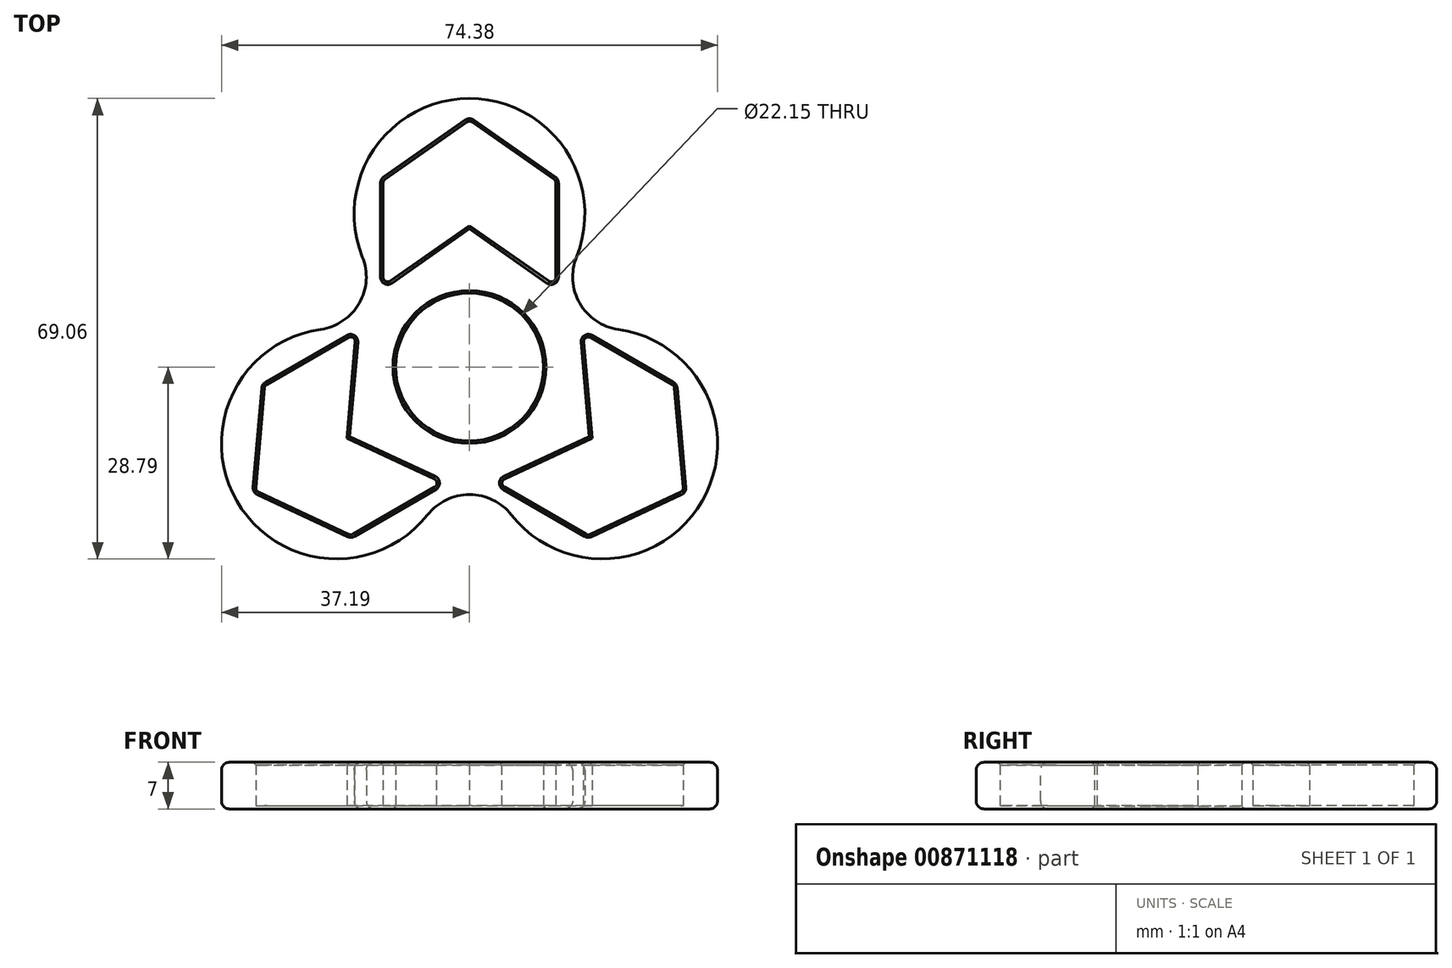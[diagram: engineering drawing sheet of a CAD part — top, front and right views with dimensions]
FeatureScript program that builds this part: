
annotation { "Feature Type Name" : "Feature", "Feature Type Description" : "" }
export const myFeature = defineFeature(function(context is Context, id is Id, definition is map)
    precondition{}
    {
        {
            var Q0;
            Q0=qCreatedBy(makeId("Top.planeOp"),FACE);
            var sketch = newSketch(context, id + "F0", { "sketchPlane" : qUnion([Q0])});
            skCircle(sketch, "E0", {"center": v(0, 0) * mm, "radius": 11.07 * mm});
            skCircle(sketch, "E1", {"center": v(0, 0) * mm, "radius": 26.5 * mm, "construction": true});
            skArc(sketch, "E2", {"start": v(-13.1, 23.03) * mm, "mid": v(-13.03, 22.75) * mm, "end": v(-12.95, 22.47) * mm, "construction": true});
            skLineSegment(sketch, "E3", {"start": v(0, 43.45) * mm, "end": v(0, 0) * mm});
            skLineSegment(sketch, "E4", {"start": v(0, 37) * mm, "end": v(12.95, 27.94) * mm});
            skLineSegment(sketch, "E5", {"start": v(12.95, 27.94) * mm, "end": v(12.95, 12.13) * mm});
            skLineSegment(sketch, "E6", {"start": v(12.95, 12.13) * mm, "end": v(0, 21.2) * mm});
            skLineSegment(sketch, "E7.MirrorCS", {"start": v(0, 37) * mm, "end": v(-12.95, 27.94) * mm});
            skLineSegment(sketch, "E8.MirrorCS", {"start": v(-12.95, 27.94) * mm, "end": v(-12.95, 12.13) * mm});
            skLineSegment(sketch, "E9.MirrorCS", {"start": v(-12.95, 12.13) * mm, "end": v(0, 21.2) * mm});
            skLineSegment(sketch, "E10.1.0", {"start": v(-32.1, -18.57) * mm, "end": v(-17.76, -25.25) * mm});
            skLineSegment(sketch, "E10.1.1", {"start": v(-17.76, -25.25) * mm, "end": v(-4.07, -17.35) * mm});
            skLineSegment(sketch, "E10.1.2", {"start": v(-4.07, -17.35) * mm, "end": v(-18.4, -10.67) * mm});
            skLineSegment(sketch, "E10.1.3", {"start": v(-17.02, 5.08) * mm, "end": v(-18.4, -10.67) * mm});
            skLineSegment(sketch, "E10.1.4", {"start": v(-30.71, -2.82) * mm, "end": v(-17.02, 5.08) * mm});
            skLineSegment(sketch, "E10.1.5", {"start": v(-32.1, -18.57) * mm, "end": v(-30.71, -2.82) * mm});
            skLineSegment(sketch, "E10.2.0", {"start": v(32.1, -18.57) * mm, "end": v(30.71, -2.82) * mm});
            skLineSegment(sketch, "E10.2.1", {"start": v(30.71, -2.82) * mm, "end": v(17.02, 5.08) * mm});
            skLineSegment(sketch, "E10.2.2", {"start": v(17.02, 5.08) * mm, "end": v(18.4, -10.67) * mm});
            skLineSegment(sketch, "E10.2.3", {"start": v(4.07, -17.35) * mm, "end": v(18.4, -10.67) * mm});
            skLineSegment(sketch, "E10.2.4", {"start": v(17.76, -25.25) * mm, "end": v(4.07, -17.35) * mm});
            skLineSegment(sketch, "E10.2.5", {"start": v(32.1, -18.57) * mm, "end": v(17.76, -25.25) * mm});
            skPoint(sketch, "E10.center", {"position": v(0, -0.05) * mm});
            skArc(sketch, "E11.trimOffspring", {"start": v(12.95, 22.47) * mm, "mid": v(13, 22.77) * mm, "end": v(13.05, 23.06) * mm, "construction": true});
            skCircle(sketch, "E12", {"center": v(0, 22.97) * mm, "radius": 17.3 * mm});
            skCircle(sketch, "E13.1.0", {"center": v(-19.9, -11.48) * mm, "radius": 17.3 * mm});
            skCircle(sketch, "E13.2.0", {"center": v(19.9, -11.48) * mm, "radius": 17.3 * mm});
            skLineSegment(sketch, "E14", {"start": v(-17.02, 5.08) * mm, "end": v(-12.95, 12.13) * mm});
            skLineSegment(sketch, "E15", {"start": v(12.95, 12.13) * mm, "end": v(17.02, 5.08) * mm});
            skLineSegment(sketch, "E16", {"start": v(4.07, -17.35) * mm, "end": v(-4.07, -17.35) * mm});
            skLineSegment(sketch, "E17", {"start": v(-7.18, -19.14) * mm, "end": v(7.18, -19.14) * mm});
            skLineSegment(sketch, "E18.1.0", {"start": v(20.13, 3.3) * mm, "end": v(12.96, 15.73) * mm});
            skLineSegment(sketch, "E18.2.0", {"start": v(-12.96, 15.73) * mm, "end": v(-20.13, 3.3) * mm});
            skPoint(sketch, "E18.center", {"position": v(0, -0.03) * mm});
            skSolve(sketch);
        }
        {
            var Q0;
            {var subQ1=sQuery(id+"F0.wireOp",EDGE,"E7.MirrorCS");Q0=makeQuery(id+"F0.imprint","IMPRINT",FACE,{"disambiguationData":[TD([[makeQuery(id+"F0.imprint","IMPRINT",EDGE,{"derivedFrom":subQ1}),-1.0]])]});}
            var Q1;
            {var subQ0=sQuery(id+"F0.wireOp",EDGE,"E4");Q1=makeQuery(id+"F0.imprint","IMPRINT",FACE,{"disambiguationData":[TD([[makeQuery(id+"F0.imprint","IMPRINT",EDGE,{"derivedFrom":subQ0}),1.0]])]});}
            var Q2;
            {var subQ5=sQuery(id+"F0.wireOp",EDGE,"E6");Q2=makeQuery(id+"F0.imprint","IMPRINT",FACE,{"disambiguationData":[TD([[makeQuery(id+"F0.imprint","IMPRINT",EDGE,{"derivedFrom":subQ5}),1.0]])]});}
            var Q3;
            {var subQ0=sQuery(id+"F0.wireOp",EDGE,"E9.MirrorCS");Q3=makeQuery(id+"F0.imprint","IMPRINT",FACE,{"disambiguationData":[TD([[makeQuery(id+"F0.imprint","IMPRINT",EDGE,{"derivedFrom":subQ0}),-1.0]])]});}
            var Q4;
            {var subQ0=sQuery(id+"F0.wireOp",EDGE,"E12");var subQ1=sQuery(id+"F0.wireOp",EDGE,"E0");var subQ2=makeQuery(id+"F0.imprint","INTERSECT",VERTEX,{"disambiguationData":[OD(1.0)],"derivedFrom":[subQ1,subQ0]});Q4=makeQuery(id+"F0.imprint","IMPRINT",FACE,{"disambiguationData":[TD([[makeQuery(id+"F0.imprint","IMPRINT",EDGE,{"disambiguationData":[TD([[subQ2,-1.0]])],"derivedFrom":subQ1}),-1.0]])]});}
            var Q5;
            {var subQ1=sQuery(id+"F0.wireOp",EDGE,"E10.1.2");Q5=makeQuery(id+"F0.imprint","IMPRINT",FACE,{"disambiguationData":[TD([[makeQuery(id+"F0.imprint","IMPRINT",EDGE,{"derivedFrom":subQ1}),-1.0]])]});}
            var Q6;
            {var subQ0=sQuery(id+"F0.wireOp",EDGE,"E13.1.0");var subQ1=sQuery(id+"F0.wireOp",EDGE,"E0");var subQ2=makeQuery(id+"F0.imprint","INTERSECT",VERTEX,{"disambiguationData":[OD(1.0)],"derivedFrom":[subQ1,subQ0]});Q6=makeQuery(id+"F0.imprint","IMPRINT",FACE,{"disambiguationData":[TD([[makeQuery(id+"F0.imprint","IMPRINT",EDGE,{"disambiguationData":[TD([[subQ2,-1.0]])],"derivedFrom":subQ1}),-1.0]])]});}
            var Q7;
            {var subQ9=sQuery(id+"F0.wireOp",EDGE,"E10.2.2");Q7=makeQuery(id+"F0.imprint","IMPRINT",FACE,{"disambiguationData":[TD([[makeQuery(id+"F0.imprint","IMPRINT",EDGE,{"derivedFrom":subQ9}),-1.0]])]});}
            var Q8;
            {var subQ0=sQuery(id+"F0.wireOp",EDGE,"E12");var subQ1=sQuery(id+"F0.wireOp",EDGE,"E0");var subQ2=makeQuery(id+"F0.imprint","INTERSECT",VERTEX,{"disambiguationData":[OD(0.0)],"derivedFrom":[subQ1,subQ0]});Q8=makeQuery(id+"F0.imprint","IMPRINT",FACE,{"disambiguationData":[TD([[makeQuery(id+"F0.imprint","IMPRINT",EDGE,{"disambiguationData":[TD([[subQ2,1.0]])],"derivedFrom":subQ1}),-1.0]])]});}
            var Q9;
            {var subQ6=sQuery(id+"F0.wireOp",EDGE,"E10.2.0");Q9=makeQuery(id+"F0.imprint","IMPRINT",FACE,{"disambiguationData":[TD([[makeQuery(id+"F0.imprint","IMPRINT",EDGE,{"derivedFrom":subQ6}),-1.0]])]});}
            var Q10;
            {var subQ7=sQuery(id+"F0.wireOp",EDGE,"E10.1.0");Q10=makeQuery(id+"F0.imprint","IMPRINT",FACE,{"disambiguationData":[TD([[makeQuery(id+"F0.imprint","IMPRINT",EDGE,{"derivedFrom":subQ7}),-1.0]])]});}
            var Q11;
            {var subQ0=sQuery(id+"F0.wireOp",EDGE,"E18.2.0");var subQ1=sQuery(id+"F0.wireOp",EDGE,"E12");var subQ2=makeQuery(id+"F0.imprint","INTERSECT",VERTEX,{"derivedFrom":[subQ1,subQ0]});Q11=makeQuery(id+"F0.imprint","IMPRINT",FACE,{"disambiguationData":[TD([[makeQuery(id+"F0.imprint","IMPRINT",EDGE,{"disambiguationData":[TD([[subQ2,-1.0]])],"derivedFrom":subQ1}),-1.0]])]});}
            var Q12;
            {var subQ0=sQuery(id+"F0.wireOp",EDGE,"E17");var subQ1=sQuery(id+"F0.wireOp",EDGE,"E13.1.0");var subQ2=makeQuery(id+"F0.imprint","INTERSECT",VERTEX,{"derivedFrom":[subQ1,subQ0]});Q12=makeQuery(id+"F0.imprint","IMPRINT",FACE,{"disambiguationData":[TD([[makeQuery(id+"F0.imprint","IMPRINT",EDGE,{"disambiguationData":[TD([[subQ2,-1.0]])],"derivedFrom":subQ1}),-1.0]])]});}
            var Q13;
            {var subQ3=sQuery(id+"F0.wireOp",EDGE,"E18.2.0");var subQ5=sQuery(id+"F0.wireOp",EDGE,"E12");var subQ7=makeQuery(id+"F0.imprint","INTERSECT",VERTEX,{"derivedFrom":[subQ5,subQ3]});Q13=makeQuery(id+"F0.imprint","IMPRINT",FACE,{"disambiguationData":[TD([[makeQuery(id+"F0.imprint","IMPRINT",EDGE,{"disambiguationData":[TD([[subQ7,-1.0]])],"derivedFrom":subQ5}),1.0]])]});}
            var Q14;
            {var subQ3=sQuery(id+"F0.wireOp",EDGE,"E18.2.0");var subQ5=sQuery(id+"F0.wireOp",EDGE,"E13.1.0");var subQ7=makeQuery(id+"F0.imprint","INTERSECT",VERTEX,{"derivedFrom":[subQ5,subQ3]});Q14=makeQuery(id+"F0.imprint","IMPRINT",FACE,{"disambiguationData":[TD([[makeQuery(id+"F0.imprint","IMPRINT",EDGE,{"disambiguationData":[TD([[subQ7,1.0]])],"derivedFrom":subQ5}),1.0]])]});}
            var Q15;
            {var subQ3=sQuery(id+"F0.wireOp",EDGE,"E17");var subQ5=sQuery(id+"F0.wireOp",EDGE,"E13.1.0");var subQ6=makeQuery(id+"F0.imprint","INTERSECT",VERTEX,{"derivedFrom":[subQ5,subQ3]});Q15=makeQuery(id+"F0.imprint","IMPRINT",FACE,{"disambiguationData":[TD([[makeQuery(id+"F0.imprint","IMPRINT",EDGE,{"disambiguationData":[TD([[subQ6,-1.0]])],"derivedFrom":subQ5}),1.0]])]});}
            var Q16;
            {var subQ3=sQuery(id+"F0.wireOp",EDGE,"E17");var subQ5=sQuery(id+"F0.wireOp",EDGE,"E13.2.0");var subQ6=makeQuery(id+"F0.imprint","INTERSECT",VERTEX,{"derivedFrom":[subQ5,subQ3]});Q16=makeQuery(id+"F0.imprint","IMPRINT",FACE,{"disambiguationData":[TD([[makeQuery(id+"F0.imprint","IMPRINT",EDGE,{"disambiguationData":[TD([[subQ6,1.0]])],"derivedFrom":subQ5}),1.0]])]});}
            var Q17;
            {var subQ3=sQuery(id+"F0.wireOp",EDGE,"E18.1.0");var subQ5=sQuery(id+"F0.wireOp",EDGE,"E12");var subQ7=makeQuery(id+"F0.imprint","INTERSECT",VERTEX,{"derivedFrom":[subQ5,subQ3]});Q17=makeQuery(id+"F0.imprint","IMPRINT",FACE,{"disambiguationData":[TD([[makeQuery(id+"F0.imprint","IMPRINT",EDGE,{"disambiguationData":[TD([[subQ7,1.0]])],"derivedFrom":subQ5}),1.0]])]});}
            var Q18;
            {var subQ3=sQuery(id+"F0.wireOp",EDGE,"E18.1.0");var subQ5=sQuery(id+"F0.wireOp",EDGE,"E13.2.0");var subQ6=makeQuery(id+"F0.imprint","INTERSECT",VERTEX,{"derivedFrom":[subQ5,subQ3]});Q18=makeQuery(id+"F0.imprint","IMPRINT",FACE,{"disambiguationData":[TD([[makeQuery(id+"F0.imprint","IMPRINT",EDGE,{"disambiguationData":[TD([[subQ6,-1.0]])],"derivedFrom":subQ5}),1.0]])]});}
            var Q19;
            {var subQ0=sQuery(id+"F0.wireOp",EDGE,"E18.1.0");var subQ1=sQuery(id+"F0.wireOp",EDGE,"E12");var subQ2=makeQuery(id+"F0.imprint","INTERSECT",VERTEX,{"derivedFrom":[subQ1,subQ0]});Q19=makeQuery(id+"F0.imprint","IMPRINT",FACE,{"disambiguationData":[TD([[makeQuery(id+"F0.imprint","IMPRINT",EDGE,{"disambiguationData":[TD([[subQ2,1.0]])],"derivedFrom":subQ1}),-1.0]])]});}
            extrude(context, id + "F1", {"entities" : qUnion([Q0, Q1, Q2, Q3, Q4, Q5, Q6, Q7, Q8, Q9, Q10, Q11, Q12, Q13, Q14, Q15, Q16, Q17, Q18, Q19]), "depth" : 7 * mm, "offsetDistance" : 25 * mm});
        }
        {
            var Q0;
            {var subQ1=sQuery(id+"F0.wireOp",EDGE,"E4");Q0=makeQuery(id+"F0.imprint","IMPRINT",FACE,{"disambiguationData":[TD([[makeQuery(id+"F0.imprint","IMPRINT",EDGE,{"derivedFrom":subQ1}),-1.0]])]});}
            var Q1;
            {var subQ3=sQuery(id+"F0.wireOp",EDGE,"E7.MirrorCS");Q1=makeQuery(id+"F0.imprint","IMPRINT",FACE,{"disambiguationData":[TD([[makeQuery(id+"F0.imprint","IMPRINT",EDGE,{"derivedFrom":subQ3}),1.0]])]});}
            var Q2;
            {var subQ3=sQuery(id+"F0.wireOp",EDGE,"E10.2.0");Q2=makeQuery(id+"F0.imprint","IMPRINT",FACE,{"disambiguationData":[TD([[makeQuery(id+"F0.imprint","IMPRINT",EDGE,{"derivedFrom":subQ3}),1.0]])]});}
            var Q3;
            {var subQ3=sQuery(id+"F0.wireOp",EDGE,"E10.1.0");Q3=makeQuery(id+"F0.imprint","IMPRINT",FACE,{"disambiguationData":[TD([[makeQuery(id+"F0.imprint","IMPRINT",EDGE,{"derivedFrom":subQ3}),1.0]])]});}
            extrude(context, id + "F2", {"entities" : qUnion([Q0, Q1, Q2, Q3]), "operationType" : NewBodyOperationType.ADD, "depth" : 0.5 * mm, "offsetDistance" : 25 * mm});
        }
        {
            var Q0;
            Q0=makeQuery(id+"F1.opExtrude","SWEPT_EDGE",EDGE,{"disambiguationData":[OSD([sQuery(id+"F0.wireOp",EDGE,"E12"),sQuery(id+"F0.wireOp",EDGE,"Zo6cloxw-RQWd-VoTV-Hmrh-WUM4IXPVoAln")])]});
            var Q1;
            Q1=makeQuery(id+"F1.opExtrude","SWEPT_EDGE",EDGE,{"disambiguationData":[OSD([sQuery(id+"F0.wireOp",EDGE,"E13.1.0"),sQuery(id+"F0.wireOp",EDGE,"Zo6cloxw-RQWd-VoTV-Hmrh-WUM4IXPVoAln")])]});
            var Q2;
            Q2=makeQuery(id+"F1.opExtrude","SWEPT_EDGE",EDGE,{"disambiguationData":[OSD([sQuery(id+"F0.wireOp",EDGE,"E13.2.0"),sQuery(id+"F0.wireOp",EDGE,"qCIH2ttQ-GXot-xXQ0-Qejf-B46ZgPa41a3F")])]});
            var Q3;
            Q3=makeQuery(id+"F1.opExtrude","SWEPT_EDGE",EDGE,{"disambiguationData":[OSD([sQuery(id+"F0.wireOp",EDGE,"E12"),sQuery(id+"F0.wireOp",EDGE,"qCIH2ttQ-GXot-xXQ0-Qejf-B46ZgPa41a3F")])]});
            var Q4;
            Q4=makeQuery(id+"F1.opExtrude","SWEPT_EDGE",EDGE,{"disambiguationData":[OSD([sQuery(id+"F0.wireOp",EDGE,"E13.2.0"),sQuery(id+"F0.wireOp",EDGE,"L0YcY93C-S2HS-15lv-KyWX-i7wwrRtpjOze")])]});
            var Q5;
            Q5=makeQuery(id+"F1.opExtrude","SWEPT_EDGE",EDGE,{"disambiguationData":[OSD([sQuery(id+"F0.wireOp",EDGE,"E13.1.0"),sQuery(id+"F0.wireOp",EDGE,"L0YcY93C-S2HS-15lv-KyWX-i7wwrRtpjOze")])]});
            fillet(context, id + "F3", {"entities" : qUnion([Q0, Q1, Q2, Q3, Q4, Q5]), "radius" : 8 * mm, "tangentPropagation" : true, "allowEdgeOverflow" : false});
        }
        {
            var Q0;
            Q0=makeQuery(id+"F1.opExtrude","CAP_EDGE",EDGE,{"disambiguationData":[OSD([sQuery(id+"F0.wireOp",EDGE,"E13.2.0")])],"isStart":true});
            var Q1;
            Q1=makeQuery(id+"F1.opExtrude","CAP_EDGE",EDGE,{"disambiguationData":[OSD([sQuery(id+"F0.wireOp",EDGE,"E13.1.0")])],"isStart":true});
            var Q2;
            Q2=makeQuery(id+"F1.opExtrude","CAP_EDGE",EDGE,{"disambiguationData":[OSD([sQuery(id+"F0.wireOp",EDGE,"E12")])],"isStart":true});
            var Q3;
            Q3=makeQuery(id+"F1.opExtrude","CAP_EDGE",EDGE,{"disambiguationData":[OSD([sQuery(id+"F0.wireOp",EDGE,"E12")])],"isStart":false});
            var Q4;
            Q4=makeQuery(id+"F1.opExtrude","CAP_EDGE",EDGE,{"disambiguationData":[OSD([sQuery(id+"F0.wireOp",EDGE,"E13.2.0")])],"isStart":false});
            var Q5;
            Q5=makeQuery(id+"F1.opExtrude","CAP_EDGE",EDGE,{"disambiguationData":[OSD([sQuery(id+"F0.wireOp",EDGE,"E13.1.0")])],"isStart":false});
            fillet(context, id + "F4", {"entities" : qUnion([Q0, Q1, Q2, Q3, Q4, Q5]), "radius" : 1.2 * mm, "tangentPropagation" : true, "allowEdgeOverflow" : false});
        }
        {
            var Q0;
            Q0=makeQuery(id+"F1.opExtrude","SWEPT_EDGE",EDGE,{"disambiguationData":[OSD([sQuery(id+"F0.wireOp",EDGE,"E10.1.0"),sQuery(id+"F0.wireOp",EDGE,"E10.1.5")])]});
            var Q1;
            Q1=makeQuery(id+"F1.opExtrude","SWEPT_EDGE",EDGE,{"disambiguationData":[OSD([sQuery(id+"F0.wireOp",EDGE,"E10.1.1"),sQuery(id+"F0.wireOp",EDGE,"E10.1.2"),sQuery(id+"F0.wireOp",EDGE,"L0YcY93C-S2HS-15lv-KyWX-i7wwrRtpjOze")])]});
            var Q2;
            Q2=makeQuery(id+"F1.opExtrude","SWEPT_EDGE",EDGE,{"disambiguationData":[OSD([sQuery(id+"F0.wireOp",EDGE,"E10.1.3"),sQuery(id+"F0.wireOp",EDGE,"E10.1.4"),sQuery(id+"F0.wireOp",EDGE,"Zo6cloxw-RQWd-VoTV-Hmrh-WUM4IXPVoAln")])]});
            var Q3;
            Q3=makeQuery(id+"F1.opExtrude","SWEPT_EDGE",EDGE,{"disambiguationData":[OSD([sQuery(id+"F0.wireOp",EDGE,"E10.1.0"),sQuery(id+"F0.wireOp",EDGE,"E10.1.1")])]});
            var Q4;
            Q4=makeQuery(id+"F1.opExtrude","SWEPT_EDGE",EDGE,{"disambiguationData":[OSD([sQuery(id+"F0.wireOp",EDGE,"E10.1.4"),sQuery(id+"F0.wireOp",EDGE,"E10.1.5")])]});
            var Q5;
            Q5=makeQuery(id+"F1.opExtrude","SWEPT_EDGE",EDGE,{"disambiguationData":[OSD([sQuery(id+"F0.wireOp",EDGE,"E10.2.3"),sQuery(id+"F0.wireOp",EDGE,"E10.2.4"),sQuery(id+"F0.wireOp",EDGE,"L0YcY93C-S2HS-15lv-KyWX-i7wwrRtpjOze")])]});
            var Q6;
            Q6=makeQuery(id+"F1.opExtrude","SWEPT_EDGE",EDGE,{"disambiguationData":[OSD([sQuery(id+"F0.wireOp",EDGE,"E10.2.4"),sQuery(id+"F0.wireOp",EDGE,"E10.2.5")])]});
            var Q7;
            Q7=makeQuery(id+"F1.opExtrude","SWEPT_EDGE",EDGE,{"disambiguationData":[OSD([sQuery(id+"F0.wireOp",EDGE,"E10.2.0"),sQuery(id+"F0.wireOp",EDGE,"E10.2.5")])]});
            var Q8;
            Q8=makeQuery(id+"F1.opExtrude","SWEPT_EDGE",EDGE,{"disambiguationData":[OSD([sQuery(id+"F0.wireOp",EDGE,"E10.2.0"),sQuery(id+"F0.wireOp",EDGE,"E10.2.1")])]});
            var Q9;
            Q9=makeQuery(id+"F1.opExtrude","SWEPT_EDGE",EDGE,{"disambiguationData":[OSD([sQuery(id+"F0.wireOp",EDGE,"E10.2.1"),sQuery(id+"F0.wireOp",EDGE,"E10.2.2"),sQuery(id+"F0.wireOp",EDGE,"qCIH2ttQ-GXot-xXQ0-Qejf-B46ZgPa41a3F")])]});
            var Q10;
            Q10=makeQuery(id+"F1.opExtrude","SWEPT_EDGE",EDGE,{"disambiguationData":[OSD([sQuery(id+"F0.wireOp",EDGE,"E5"),sQuery(id+"F0.wireOp",EDGE,"E6"),sQuery(id+"F0.wireOp",EDGE,"qCIH2ttQ-GXot-xXQ0-Qejf-B46ZgPa41a3F")])]});
            var Q11;
            Q11=makeQuery(id+"F1.opExtrude","SWEPT_EDGE",EDGE,{"disambiguationData":[OSD([sQuery(id+"F0.wireOp",EDGE,"E8.MirrorCS"),sQuery(id+"F0.wireOp",EDGE,"E9.MirrorCS"),sQuery(id+"F0.wireOp",EDGE,"Zo6cloxw-RQWd-VoTV-Hmrh-WUM4IXPVoAln")])]});
            var Q12;
            Q12=makeQuery(id+"F1.opExtrude","SWEPT_EDGE",EDGE,{"disambiguationData":[OSD([sQuery(id+"F0.wireOp",EDGE,"E4"),sQuery(id+"F0.wireOp",EDGE,"E5")])]});
            var Q13;
            Q13=makeQuery(id+"F1.opExtrude","SWEPT_EDGE",EDGE,{"disambiguationData":[OSD([sQuery(id+"F0.wireOp",EDGE,"E3"),sQuery(id+"F0.wireOp",EDGE,"E4"),sQuery(id+"F0.wireOp",EDGE,"E7.MirrorCS")])]});
            var Q14;
            Q14=makeQuery(id+"F1.opExtrude","SWEPT_EDGE",EDGE,{"disambiguationData":[OSD([sQuery(id+"F0.wireOp",EDGE,"E7.MirrorCS"),sQuery(id+"F0.wireOp",EDGE,"E8.MirrorCS")])]});
            fillet(context, id + "F5", {"entities" : qUnion([Q0, Q1, Q2, Q3, Q4, Q5, Q6, Q7, Q8, Q9, Q10, Q11, Q12, Q13, Q14]), "radius" : 0.7 * mm, "tangentPropagation" : true, "allowEdgeOverflow" : false});
        }
        {
            var Q0;
            Q0=makeQuery(id+"F1.opExtrude","CAP_FACE",FACE,{"disambiguationData":[OSD([sQuery(id+"F0.wireOp",EDGE,"E0"),sQuery(id+"F0.wireOp",EDGE,"E4"),sQuery(id+"F0.wireOp",EDGE,"E5"),sQuery(id+"F0.wireOp",EDGE,"E6"),sQuery(id+"F0.wireOp",EDGE,"E7.MirrorCS"),sQuery(id+"F0.wireOp",EDGE,"E8.MirrorCS"),sQuery(id+"F0.wireOp",EDGE,"E9.MirrorCS"),sQuery(id+"F0.wireOp",EDGE,"E10.1.0"),sQuery(id+"F0.wireOp",EDGE,"E10.1.1"),sQuery(id+"F0.wireOp",EDGE,"E10.1.2"),sQuery(id+"F0.wireOp",EDGE,"E10.1.3"),sQuery(id+"F0.wireOp",EDGE,"E10.1.4"),sQuery(id+"F0.wireOp",EDGE,"E10.1.5"),sQuery(id+"F0.wireOp",EDGE,"E10.2.0"),sQuery(id+"F0.wireOp",EDGE,"E10.2.1"),sQuery(id+"F0.wireOp",EDGE,"E10.2.2"),sQuery(id+"F0.wireOp",EDGE,"E10.2.3"),sQuery(id+"F0.wireOp",EDGE,"E10.2.4"),sQuery(id+"F0.wireOp",EDGE,"E10.2.5"),sQuery(id+"F0.wireOp",EDGE,"E12"),sQuery(id+"F0.wireOp",EDGE,"E13.1.0"),sQuery(id+"F0.wireOp",EDGE,"E13.2.0"),sQuery(id+"F0.wireOp",EDGE,"qCIH2ttQ-GXot-xXQ0-Qejf-B46ZgPa41a3F"),sQuery(id+"F0.wireOp",EDGE,"Zo6cloxw-RQWd-VoTV-Hmrh-WUM4IXPVoAln"),sQuery(id+"F0.wireOp",EDGE,"L0YcY93C-S2HS-15lv-KyWX-i7wwrRtpjOze")])],"isStart":true});
            var Q1;
            Q1=makeQuery(id+"F1.opExtrude","CAP_FACE",FACE,{"disambiguationData":[OSD([sQuery(id+"F0.wireOp",EDGE,"E0"),sQuery(id+"F0.wireOp",EDGE,"E4"),sQuery(id+"F0.wireOp",EDGE,"E5"),sQuery(id+"F0.wireOp",EDGE,"E6"),sQuery(id+"F0.wireOp",EDGE,"E7.MirrorCS"),sQuery(id+"F0.wireOp",EDGE,"E8.MirrorCS"),sQuery(id+"F0.wireOp",EDGE,"E9.MirrorCS"),sQuery(id+"F0.wireOp",EDGE,"E10.1.0"),sQuery(id+"F0.wireOp",EDGE,"E10.1.1"),sQuery(id+"F0.wireOp",EDGE,"E10.1.2"),sQuery(id+"F0.wireOp",EDGE,"E10.1.3"),sQuery(id+"F0.wireOp",EDGE,"E10.1.4"),sQuery(id+"F0.wireOp",EDGE,"E10.1.5"),sQuery(id+"F0.wireOp",EDGE,"E10.2.0"),sQuery(id+"F0.wireOp",EDGE,"E10.2.1"),sQuery(id+"F0.wireOp",EDGE,"E10.2.2"),sQuery(id+"F0.wireOp",EDGE,"E10.2.3"),sQuery(id+"F0.wireOp",EDGE,"E10.2.4"),sQuery(id+"F0.wireOp",EDGE,"E10.2.5"),sQuery(id+"F0.wireOp",EDGE,"E12"),sQuery(id+"F0.wireOp",EDGE,"E13.1.0"),sQuery(id+"F0.wireOp",EDGE,"E13.2.0"),sQuery(id+"F0.wireOp",EDGE,"qCIH2ttQ-GXot-xXQ0-Qejf-B46ZgPa41a3F"),sQuery(id+"F0.wireOp",EDGE,"Zo6cloxw-RQWd-VoTV-Hmrh-WUM4IXPVoAln"),sQuery(id+"F0.wireOp",EDGE,"L0YcY93C-S2HS-15lv-KyWX-i7wwrRtpjOze")])],"isStart":false});
            chamfer(context, id + "F6", {"entities" : qUnion([Q0, Q1]), "width" : 0.4 * mm, "tangentPropagation" : true});
        }
    });
